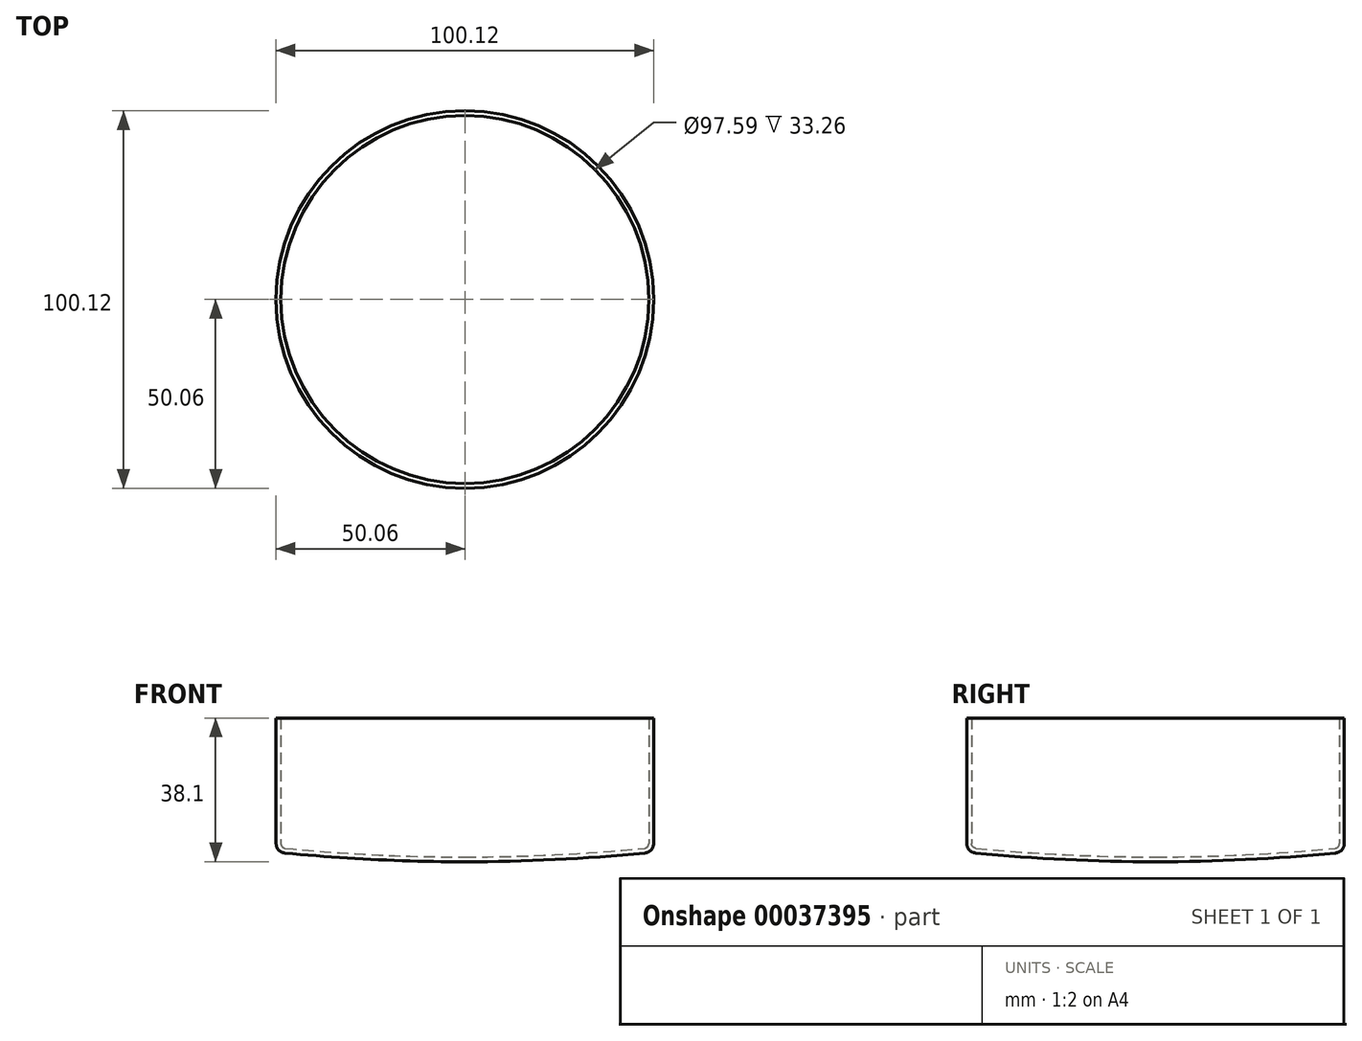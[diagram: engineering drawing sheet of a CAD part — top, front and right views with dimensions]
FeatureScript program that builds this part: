
annotation { "Feature Type Name" : "Feature", "Feature Type Description" : "" }
export const myFeature = defineFeature(function(context is Context, id is Id, definition is map)
    precondition{}
    {
        {
            var Q0;
            Q0=qCreatedBy(makeId("Front.planeOp"),FACE);
            var sketch = newSketch(context, id + "F0", { "sketchPlane" : qUnion([Q0])});
            skLineSegment(sketch, "E0", {"start": v(-48.8, 38.1) * mm, "end": v(-50.06, 38.1) * mm});
            skLineSegment(sketch, "E1", {"start": v(-50.06, 38.1) * mm, "end": v(-50.06, 4.84) * mm});
            skArc(sketch, "E2", {"start": v(-47.77, 2.31) * mm, "mid": v(-23.91, 0.58) * mm, "end": v(0, 0) * mm});
            skPoint(sketch, "E3.visualSharp", {"position": v(-50.06, 2.54) * mm});
            skArc(sketch, "E3.filletArc", {"start": v(-50.06, 4.84) * mm, "mid": v(-49.4, 3.13) * mm, "end": v(-47.77, 2.31) * mm});
            skLineSegment(sketch, "E4", {"start": v(-48.8, 38.1) * mm, "end": v(-48.8, 4.84) * mm});
            skArc(sketch, "E5", {"start": v(-48.8, 4.84) * mm, "mid": v(-48.46, 3.99) * mm, "end": v(-47.65, 3.58) * mm});
            skArc(sketch, "E6", {"start": v(-47.65, 3.58) * mm, "mid": v(-23.85, 1.85) * mm, "end": v(0, 1.27) * mm});
            skLineSegment(sketch, "E7", {"start": v(0, 0) * mm, "end": v(0, 1.27) * mm});
            skSolve(sketch);
        }
        {
            var Q0;
            Q0 = qSketchRegion(id + "F0", true);
            var Q1;
            Q1=sQuery(id+"F0.wireOp",EDGE,"E7");
            revolve(context, id + "F1", {"entities" : qUnion([Q0]), "axis" : qUnion([Q1]), "revolveType" : RevolveType.FULL});
        }
    });
